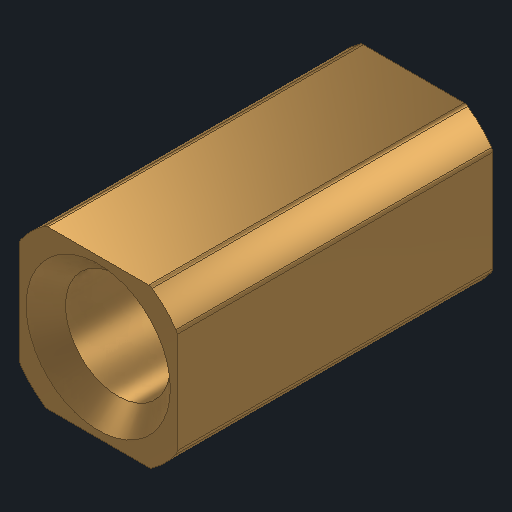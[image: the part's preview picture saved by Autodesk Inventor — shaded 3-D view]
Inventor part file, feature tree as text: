
AUTODESK INVENTOR PART (.ipt)
format: ipt  version: 2025 (Build 290162000, 162)  size: 161,792 bytes
history: native  units: in
note: dims shown in document units (in); Inventor stores cm internally (conversion verified against a paired STEP export)
features: other x3, sketch x2
ambient origin geometry x8: Origin, YZ Plane, XZ Plane, XY Plane, X Axis, Y Axis, Z Axis, Center Point
bodies: Solid1 (feature_tree)
feature tree (5):
  other  "HS Shaft Adapter Circle.ipt"
  other  "Solid1::HS Shaft Adapter Circle.ipt"
  other  "TaggingFeature1"
  sketch  "Sketch1"  dims[d0=0.3937in]
  sketch  "Sketch2"
